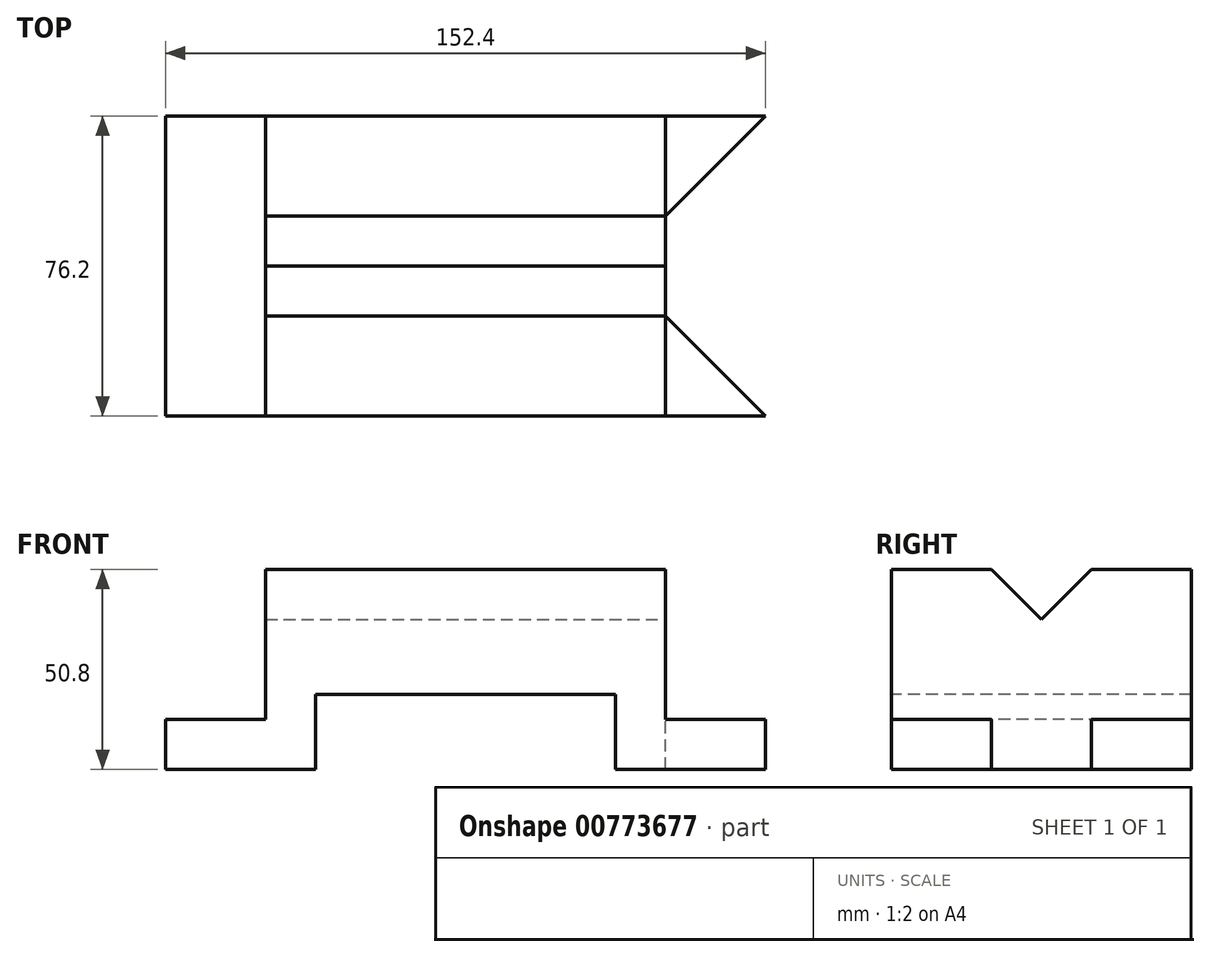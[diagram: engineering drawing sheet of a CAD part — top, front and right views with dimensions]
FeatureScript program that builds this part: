
annotation { "Feature Type Name" : "Feature", "Feature Type Description" : "" }
export const myFeature = defineFeature(function(context is Context, id is Id, definition is map)
    precondition{}
    {
        {
            var Q0;
            Q0=qCreatedBy(makeId("Front.planeOp"),FACE);
            var sketch = newSketch(context, id + "F0", { "sketchPlane" : qUnion([Q0])});
            skLineSegment(sketch, "E0", {"start": v(0, 0) * mm, "end": v(152.4, 0) * mm});
            skLineSegment(sketch, "E1", {"start": v(152.4, 0) * mm, "end": v(152.4, 50.8) * mm});
            skLineSegment(sketch, "E2", {"start": v(152.4, 50.8) * mm, "end": v(0, 50.8) * mm});
            skLineSegment(sketch, "E3", {"start": v(0, 50.8) * mm, "end": v(0, 0) * mm});
            skSolve(sketch);
        }
        {
            var Q0;
            Q0=makeQuery(id+"F0.imprint","IMPRINT",FACE,{"disambiguationData":[TD([[makeQuery(id+"F0.imprint","IMPRINT",EDGE,{"derivedFrom":sQuery(id+"F0.wireOp",EDGE,"E0")}),1.0]])]});
            extrude(context, id + "F1", {"entities" : qUnion([Q0]), "depth" : 76.2 * mm, "offsetDistance" : 25.4 * mm});
        }
        {
            var Q0;
            Q0=makeQuery(id+"F1.opExtrude","SWEPT_FACE",FACE,{"disambiguationData":[OSD([sQuery(id+"F0.wireOp",EDGE,"E1")])]});
            var sketch = newSketch(context, id + "F2", { "sketchPlane" : qUnion([Q0])});
            skLineSegment(sketch, "E4", {"start": v(-76.2, 50.8) * mm, "end": v(-50.8, 50.8) * mm});
            skLineSegment(sketch, "E5", {"start": v(0, 50.8) * mm, "end": v(-25.4, 50.8) * mm});
            skLineSegment(sketch, "E6", {"start": v(-25.4, 50.8) * mm, "end": v(-38.1, 50.8) * mm});
            skLineSegment(sketch, "E7", {"start": v(-38.1, 50.8) * mm, "end": v(-38.1, 38.1) * mm});
            skLineSegment(sketch, "E8", {"start": v(-38.1, 38.1) * mm, "end": v(-50.8, 50.8) * mm});
            skLineSegment(sketch, "E9", {"start": v(-38.1, 38.1) * mm, "end": v(-25.4, 50.8) * mm});
            skSolve(sketch);
        }
        {
            var Q0;
            {var subQ0=sQuery(id+"F2.wireOp",EDGE,"E7");Q0=makeQuery(id+"F2.imprint","IMPRINT",FACE,{"disambiguationData":[TD([[makeQuery(id+"F2.imprint","IMPRINT",EDGE,{"derivedFrom":subQ0}),-1.0]])]});}
            var Q1;
            Q1=makeQuery(id+"F2.imprint","IMPRINT",FACE,{"disambiguationData":[TD([[makeQuery(id+"F2.imprint","IMPRINT",EDGE,{"derivedFrom":sQuery(id+"F2.wireOp",EDGE,"E6")}),-1.0]])]});
            extrude(context, id + "F3", {"entities" : qUnion([Q0, Q1]), "operationType" : NewBodyOperationType.REMOVE, "oppositeDirection" : true, "depth" : 203.2 * mm, "offsetDistance" : 25.4 * mm});
        }
        {
            var Q0;
            Q0=makeQuery(id+"F1.opExtrude","CAP_FACE",FACE,{"disambiguationData":[OSD([sQuery(id+"F0.wireOp",EDGE,"E0"),sQuery(id+"F0.wireOp",EDGE,"E1"),sQuery(id+"F0.wireOp",EDGE,"E2"),sQuery(id+"F0.wireOp",EDGE,"E3")])],"isStart":false});
            var sketch = newSketch(context, id + "F4", { "sketchPlane" : qUnion([Q0])});
            skLineSegment(sketch, "E10", {"start": v(0, 0) * mm, "end": v(0, 12.7) * mm});
            skLineSegment(sketch, "E11", {"start": v(0, 12.7) * mm, "end": v(25.4, 12.7) * mm});
            skLineSegment(sketch, "E12", {"start": v(25.4, 12.7) * mm, "end": v(25.4, 50.8) * mm});
            skSolve(sketch);
        }
        {
            var Q0;
            {var subQ0=sQuery(id+"F4.wireOp",EDGE,"E11");Q0=makeQuery(id+"F4.imprint","IMPRINT",FACE,{"disambiguationData":[TD([[makeQuery(id+"F4.imprint","IMPRINT",EDGE,{"derivedFrom":subQ0}),1.0]])]});}
            extrude(context, id + "F5", {"entities" : qUnion([Q0]), "operationType" : NewBodyOperationType.REMOVE, "oppositeDirection" : true, "depth" : 101.6 * mm, "offsetDistance" : 25.4 * mm});
        }
        {
            var Q0;
            Q0=makeQuery(id+"F1.opExtrude","CAP_FACE",FACE,{"disambiguationData":[OSD([sQuery(id+"F0.wireOp",EDGE,"E0"),sQuery(id+"F0.wireOp",EDGE,"E1"),sQuery(id+"F0.wireOp",EDGE,"E2"),sQuery(id+"F0.wireOp",EDGE,"E3")])],"isStart":false});
            var sketch = newSketch(context, id + "F6", { "sketchPlane" : qUnion([Q0])});
            skLineSegment(sketch, "E13", {"start": v(152.4, 0) * mm, "end": v(152.4, 12.7) * mm});
            skLineSegment(sketch, "E14", {"start": v(152.4, 12.7) * mm, "end": v(127, 12.7) * mm});
            skLineSegment(sketch, "E15", {"start": v(127, 12.7) * mm, "end": v(127, 50.8) * mm});
            skSolve(sketch);
        }
        {
            var Q0;
            {var subQ0=sQuery(id+"F6.wireOp",EDGE,"E14");Q0=makeQuery(id+"F6.imprint","IMPRINT",FACE,{"disambiguationData":[TD([[makeQuery(id+"F6.imprint","IMPRINT",EDGE,{"derivedFrom":subQ0}),-1.0]])]});}
            extrude(context, id + "F7", {"entities" : qUnion([Q0]), "operationType" : NewBodyOperationType.REMOVE, "oppositeDirection" : true, "depth" : 101.6 * mm, "offsetDistance" : 25.4 * mm});
        }
        {
            var Q0;
            Q0=makeQuery(id+"F7.boolean.opBoolean","COPY",FACE,{"derivedFrom":makeQuery(id+"F7.opExtrude","SWEPT_FACE",FACE,{"disambiguationData":[OSD([sQuery(id+"F6.wireOp",EDGE,"E14")])]})});
            var sketch = newSketch(context, id + "F8", { "sketchPlane" : qUnion([Q0])});
            skLineSegment(sketch, "E16", {"start": v(152.4, 0) * mm, "end": v(152.4, -25.4) * mm});
            skLineSegment(sketch, "E17", {"start": v(152.4, -76.2) * mm, "end": v(152.4, -50.8) * mm});
            skLineSegment(sketch, "E18", {"start": v(152.4, -50.8) * mm, "end": v(127, -50.8) * mm});
            skLineSegment(sketch, "E19", {"start": v(152.4, -25.4) * mm, "end": v(127, -25.4) * mm});
            skLineSegment(sketch, "E20", {"start": v(152.4, -76.2) * mm, "end": v(127, -50.8) * mm});
            skLineSegment(sketch, "E21", {"start": v(127, -25.4) * mm, "end": v(152.4, 0) * mm});
            skSolve(sketch);
        }
        {
            var Q0;
            Q0=makeQuery(id+"F8.imprint","IMPRINT",FACE,{"disambiguationData":[TD([[makeQuery(id+"F8.imprint","IMPRINT",EDGE,{"derivedFrom":sQuery(id+"F8.wireOp",EDGE,"E17")}),-1.0]])]});
            var Q1;
            {var subQ0=sQuery(id+"F8.wireOp",EDGE,"E18");Q1=makeQuery(id+"F8.imprint","IMPRINT",FACE,{"disambiguationData":[TD([[makeQuery(id+"F8.imprint","IMPRINT",EDGE,{"derivedFrom":subQ0}),-1.0]])]});}
            var Q2;
            Q2=makeQuery(id+"F8.imprint","IMPRINT",FACE,{"disambiguationData":[TD([[makeQuery(id+"F8.imprint","IMPRINT",EDGE,{"derivedFrom":sQuery(id+"F8.wireOp",EDGE,"E16")}),-1.0]])]});
            extrude(context, id + "F9", {"entities" : qUnion([Q0, Q1, Q2]), "operationType" : NewBodyOperationType.REMOVE, "oppositeDirection" : true, "depth" : 25.4 * mm, "offsetDistance" : 25.4 * mm});
        }
        {
            var Q0;
            Q0=makeQuery(id+"F1.opExtrude","CAP_FACE",FACE,{"disambiguationData":[OSD([sQuery(id+"F0.wireOp",EDGE,"E0"),sQuery(id+"F0.wireOp",EDGE,"E1"),sQuery(id+"F0.wireOp",EDGE,"E2"),sQuery(id+"F0.wireOp",EDGE,"E3")])],"isStart":false});
            var sketch = newSketch(context, id + "F10", { "sketchPlane" : qUnion([Q0])});
            skLineSegment(sketch, "E22", {"start": v(0, 0) * mm, "end": v(38.1, 0) * mm});
            skLineSegment(sketch, "E23", {"start": v(38.1, 0) * mm, "end": v(38.1, 19.05) * mm});
            skLineSegment(sketch, "E24", {"start": v(38.1, 19.05) * mm, "end": v(114.3, 19.05) * mm});
            skLineSegment(sketch, "E25", {"start": v(114.3, 19.05) * mm, "end": v(114.3, 0) * mm});
            skSolve(sketch);
        }
        {
            var Q0;
            {var subQ0=sQuery(id+"F10.wireOp",EDGE,"E23");Q0=makeQuery(id+"F10.imprint","IMPRINT",FACE,{"disambiguationData":[TD([[makeQuery(id+"F10.imprint","IMPRINT",EDGE,{"derivedFrom":subQ0}),-1.0]])]});}
            extrude(context, id + "F11", {"entities" : qUnion([Q0]), "operationType" : NewBodyOperationType.REMOVE, "oppositeDirection" : true, "depth" : 127 * mm, "offsetDistance" : 25.4 * mm});
        }
    });
